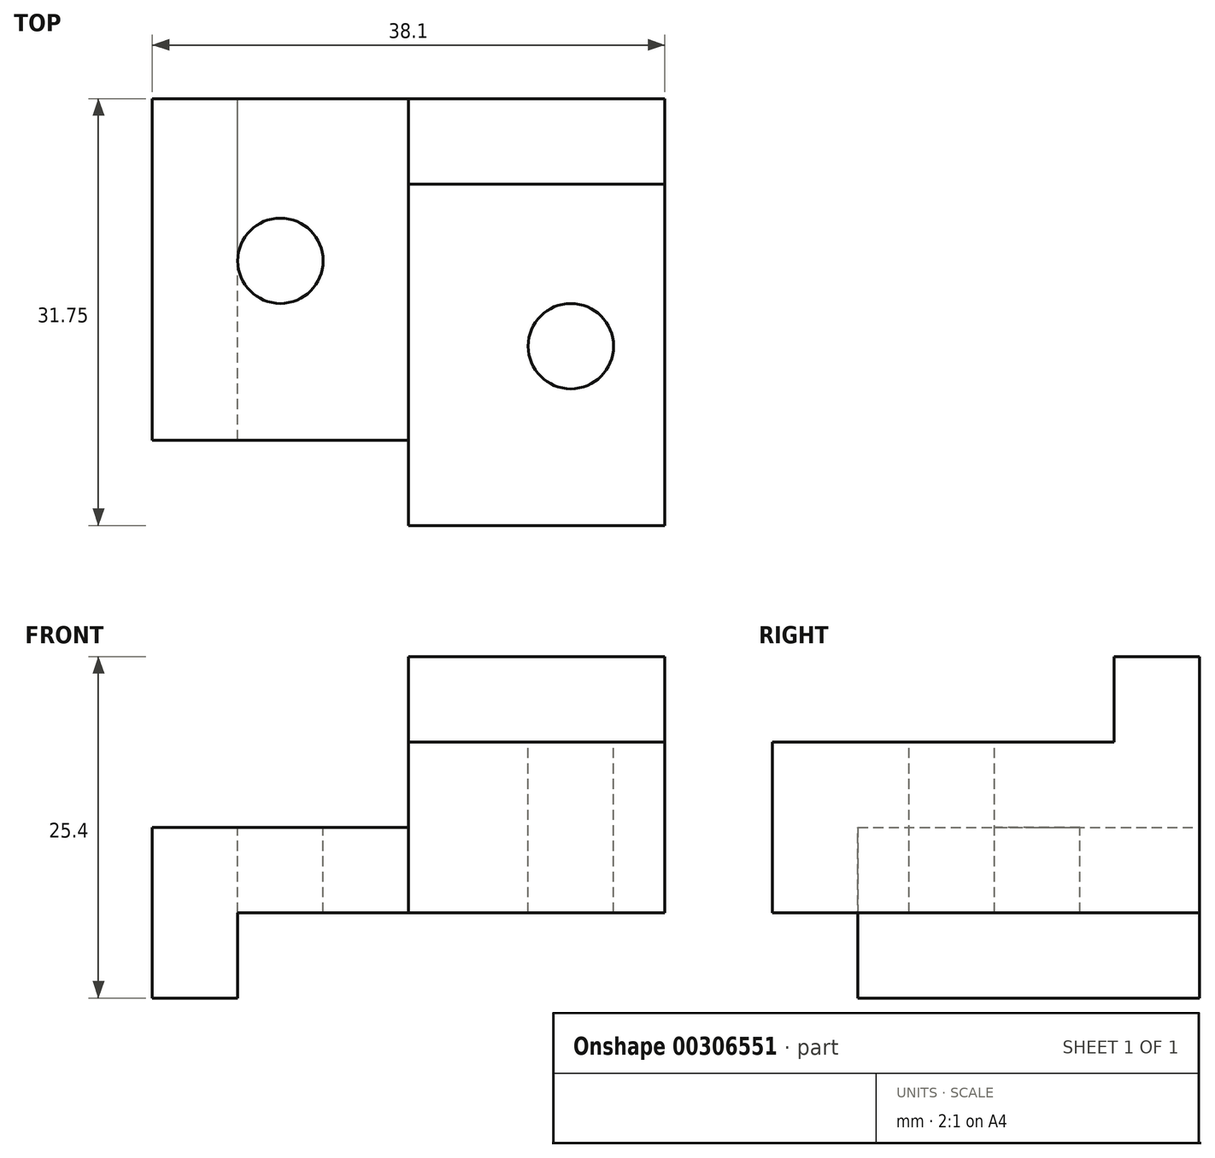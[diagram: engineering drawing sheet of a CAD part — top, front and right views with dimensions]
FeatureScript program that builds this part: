
annotation { "Feature Type Name" : "Feature", "Feature Type Description" : "" }
export const myFeature = defineFeature(function(context is Context, id is Id, definition is map)
    precondition{}
    {
        {
            var Q0;
            Q0=qCreatedBy(makeId("Front.planeOp"),FACE);
            var sketch = newSketch(context, id + "F0", { "sketchPlane" : qUnion([Q0])});
            skLineSegment(sketch, "E0", {"start": v(0, 0) * mm, "end": v(0, 12.7) * mm});
            skLineSegment(sketch, "E1", {"start": v(0, 12.7) * mm, "end": v(19.05, 12.7) * mm});
            skLineSegment(sketch, "E2", {"start": v(19.05, 12.7) * mm, "end": v(19.05, 19.05) * mm});
            skLineSegment(sketch, "E3", {"start": v(19.05, 19.05) * mm, "end": v(38.1, 19.05) * mm});
            skLineSegment(sketch, "E4", {"start": v(38.1, 19.05) * mm, "end": v(38.1, 6.35) * mm});
            skLineSegment(sketch, "E5", {"start": v(38.1, 6.35) * mm, "end": v(6.35, 6.35) * mm});
            skLineSegment(sketch, "E6", {"start": v(6.35, 6.35) * mm, "end": v(6.35, 0) * mm});
            skLineSegment(sketch, "E7", {"start": v(6.35, 0) * mm, "end": v(0, 0) * mm});
            skSolve(sketch);
        }
        {
            var Q0;
            Q0=makeQuery(id+"F0.imprint","IMPRINT",FACE,{"disambiguationData":[TD([[makeQuery(id+"F0.imprint","IMPRINT",EDGE,{"derivedFrom":sQuery(id+"F0.wireOp",EDGE,"E0")}),-1.0]])]});
            extrude(context, id + "F1", {"entities" : qUnion([Q0]), "depth" : 31.75 * mm});
        }
        {
            var Q0;
            Q0=makeQuery(id+"F1.opExtrude","CAP_FACE",FACE,{"disambiguationData":[OSD([sQuery(id+"F0.wireOp",EDGE,"E0"),sQuery(id+"F0.wireOp",EDGE,"E1"),sQuery(id+"F0.wireOp",EDGE,"E2"),sQuery(id+"F0.wireOp",EDGE,"E3"),sQuery(id+"F0.wireOp",EDGE,"E4"),sQuery(id+"F0.wireOp",EDGE,"E5"),sQuery(id+"F0.wireOp",EDGE,"E6"),sQuery(id+"F0.wireOp",EDGE,"E7")])],"isStart":false});
            var sketch = newSketch(context, id + "F2", { "sketchPlane" : qUnion([Q0])});
            skLineSegment(sketch, "E8", {"start": v(19.05, 12.7) * mm, "end": v(19.05, 6.35) * mm});
            skLineSegment(sketch, "E9", {"start": v(19.05, 6.35) * mm, "end": v(6.35, 6.35) * mm});
            skLineSegment(sketch, "E10", {"start": v(6.35, 6.35) * mm, "end": v(6.35, 0) * mm});
            skLineSegment(sketch, "E11", {"start": v(6.35, 0) * mm, "end": v(0, 0) * mm});
            skLineSegment(sketch, "E12", {"start": v(0, 0) * mm, "end": v(0, 12.7) * mm});
            skLineSegment(sketch, "E13", {"start": v(0, 12.7) * mm, "end": v(19.05, 12.7) * mm});
            skSolve(sketch);
        }
        {
            var Q0;
            Q0=makeQuery(id+"F2.imprint","IMPRINT",FACE,{"disambiguationData":[TD([[makeQuery(id+"F2.imprint","IMPRINT",EDGE,{"derivedFrom":sQuery(id+"F2.wireOp",EDGE,"E8")}),-1.0]])]});
            extrude(context, id + "F3", {"entities" : qUnion([Q0]), "operationType" : NewBodyOperationType.REMOVE, "oppositeDirection" : true, "depth" : 6.35 * mm});
        }
        {
            var Q0;
            Q0=makeQuery(id+"F1.opExtrude","SWEPT_FACE",FACE,{"disambiguationData":[OSD([sQuery(id+"F0.wireOp",EDGE,"E3")])]});
            var sketch = newSketch(context, id + "F4", { "sketchPlane" : qUnion([Q0])});
            skLineSegment(sketch, "E14", {"start": v(19.05, 0) * mm, "end": v(19.05, -6.35) * mm});
            skLineSegment(sketch, "E15", {"start": v(19.05, -6.35) * mm, "end": v(38.1, -6.35) * mm});
            skLineSegment(sketch, "E16", {"start": v(38.1, -6.35) * mm, "end": v(38.1, 0) * mm});
            skLineSegment(sketch, "E17", {"start": v(38.1, 0) * mm, "end": v(19.05, 0) * mm});
            skCircle(sketch, "E18", {"center": v(31.12, -18.41) * mm, "radius": 3.18 * mm});
            skCircle(sketch, "E19", {"center": v(9.53, -12.06) * mm, "radius": 3.18 * mm});
            skSolve(sketch);
        }
        {
            var Q0;
            Q0=makeQuery(id+"F4.imprint","IMPRINT",FACE,{"disambiguationData":[TD([[makeQuery(id+"F4.imprint","IMPRINT",EDGE,{"derivedFrom":sQuery(id+"F4.wireOp",EDGE,"E14")}),-1.0]])]});
            extrude(context, id + "F5", {"entities" : qUnion([Q0]), "operationType" : NewBodyOperationType.ADD, "depth" : 6.35 * mm});
        }
        {
            var Q0;
            Q0=makeQuery(id+"F4.imprint","IMPRINT",FACE,{"disambiguationData":[TD([[makeQuery(id+"F4.imprint","IMPRINT",EDGE,{"derivedFrom":sQuery(id+"F4.wireOp",EDGE,"E18")}),1.0]])]});
            var Q1;
            Q1=makeQuery(id+"F4.imprint","IMPRINT",FACE,{"disambiguationData":[TD([[makeQuery(id+"F4.imprint","IMPRINT",EDGE,{"derivedFrom":sQuery(id+"F4.wireOp",EDGE,"E19")}),1.0]])]});
            extrude(context, id + "F6", {"entities" : qUnion([Q0, Q1]), "operationType" : NewBodyOperationType.REMOVE, "endBound" : BoundingType.THROUGH_ALL, "oppositeDirection" : true, "depth" : 25.4 * mm});
        }
    });
